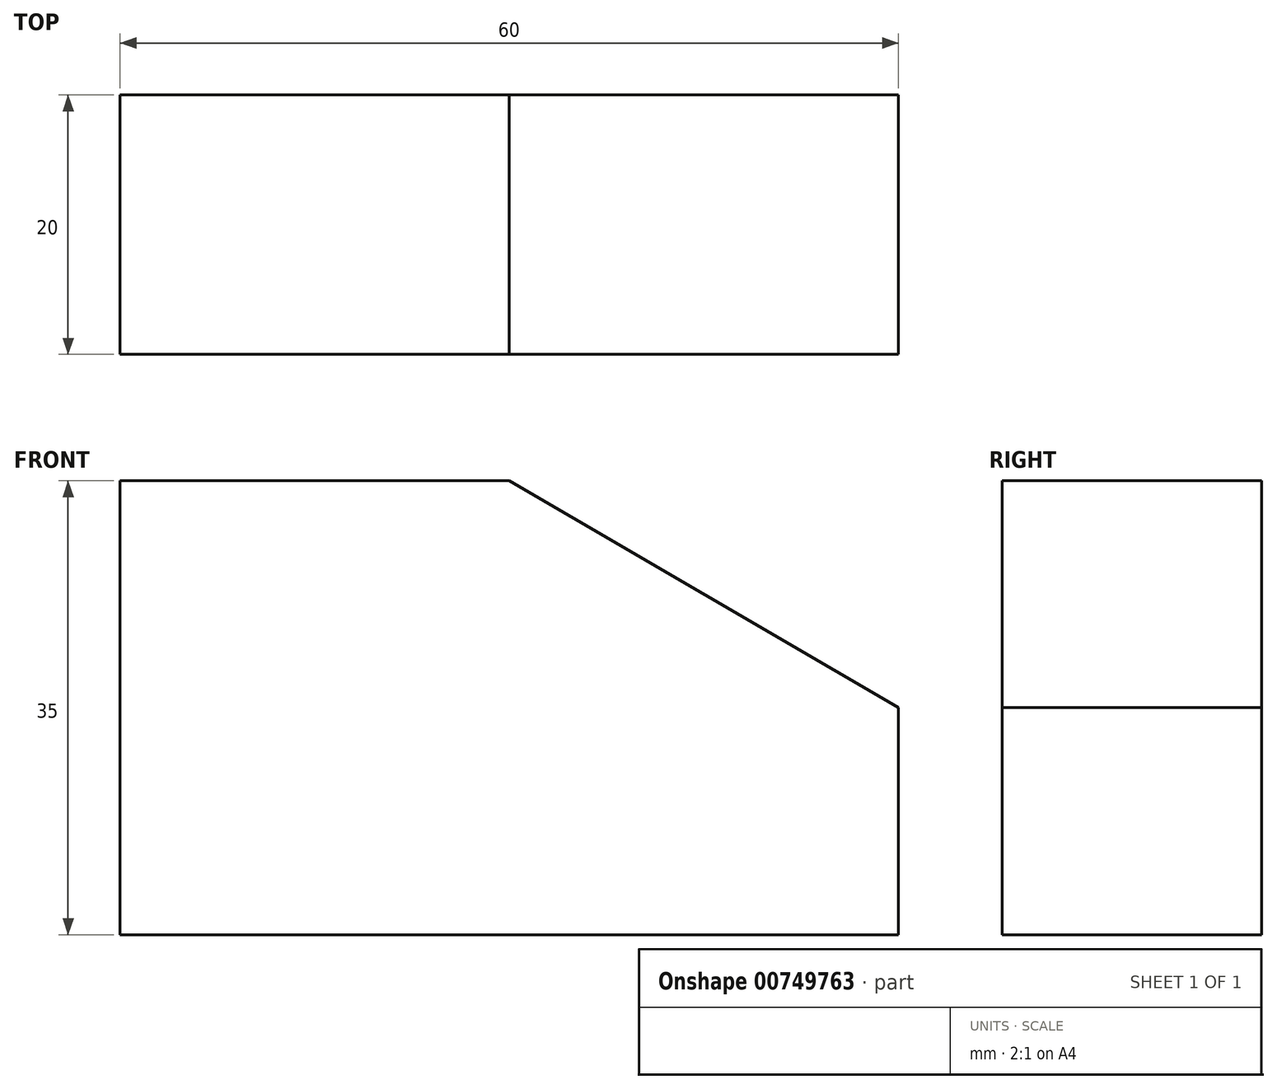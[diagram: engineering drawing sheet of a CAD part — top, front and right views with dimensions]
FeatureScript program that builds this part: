
annotation { "Feature Type Name" : "Feature", "Feature Type Description" : "" }
export const myFeature = defineFeature(function(context is Context, id is Id, definition is map)
    precondition{}
    {
        {
            var Q0;
            Q0=qCreatedBy(makeId("Front.planeOp"),FACE);
            var sketch = newSketch(context, id + "F0", { "sketchPlane" : qUnion([Q0])});
            skLineSegment(sketch, "E0.bottom", {"start": v(0, 0) * mm, "end": v(60, 0) * mm});
            skLineSegment(sketch, "E0.top", {"start": v(0, 35) * mm, "end": v(60, 35) * mm});
            skLineSegment(sketch, "E0.left", {"start": v(0, 0) * mm, "end": v(0, 35) * mm});
            skLineSegment(sketch, "E0.right", {"start": v(60, 0) * mm, "end": v(60, 35) * mm});
            skSolve(sketch);
        }
        {
            var Q0;
            Q0 = qSketchRegion(id + "F0", true);
            extrude(context, id + "F1", {"entities" : qUnion([Q0]), "depth" : 20 * mm, "offsetDistance" : 25 * mm});
        }
        {
            var Q0;
            Q0=makeQuery(id+"F1.opExtrude","CAP_FACE",FACE,{"disambiguationData":[OSD([sQuery(id+"F0.wireOp",EDGE,"E0.bottom"),sQuery(id+"F0.wireOp",EDGE,"E0.top"),sQuery(id+"F0.wireOp",EDGE,"E0.left"),sQuery(id+"F0.wireOp",EDGE,"E0.right")])],"isStart":false});
            var sketch = newSketch(context, id + "F2", { "sketchPlane" : qUnion([Q0])});
            skLineSegment(sketch, "E1", {"start": v(30, 35) * mm, "end": v(60, 17.5) * mm});
            skSolve(sketch);
        }
        {
            var Q0;
            Q0 = qSketchRegion(id + "F2", true);
            var Q1;
            {var subQ0=sQuery(id+"F2.wireOp",EDGE,"E1");Q1=makeQuery(id+"F2.imprint","IMPRINT",FACE,{"disambiguationData":[TD([[makeQuery(id+"F2.imprint","IMPRINT",EDGE,{"derivedFrom":subQ0}),1.0]])]});}
            extrude(context, id + "F3", {"entities" : qUnion([Q0, Q1]), "operationType" : NewBodyOperationType.REMOVE, "oppositeDirection" : true, "depth" : 250.9 * mm, "offsetDistance" : 25 * mm});
        }
    });
